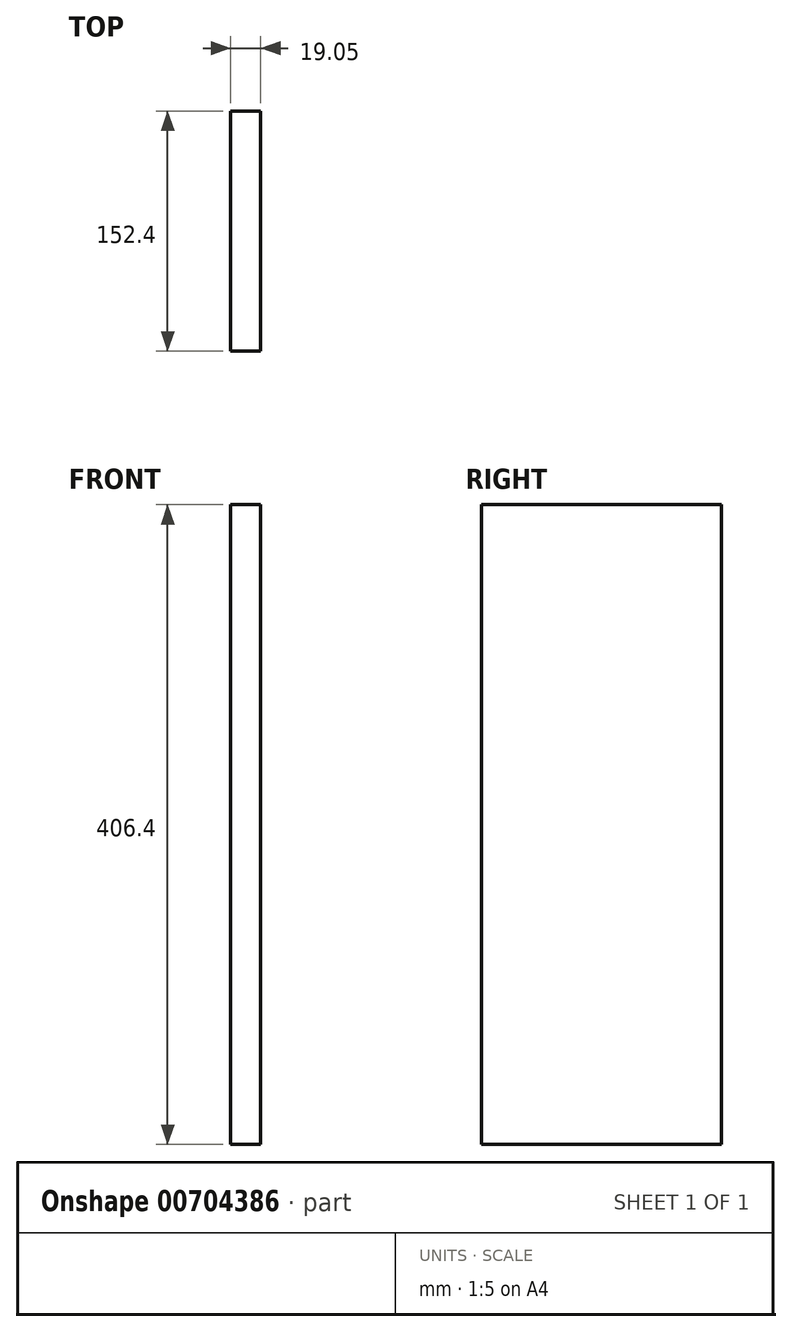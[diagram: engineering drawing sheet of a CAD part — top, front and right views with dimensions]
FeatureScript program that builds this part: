
annotation { "Feature Type Name" : "Feature", "Feature Type Description" : "" }
export const myFeature = defineFeature(function(context is Context, id is Id, definition is map)
    precondition{}
    {
        {
            var Q0;
            Q0=qCreatedBy(makeId("Right.planeOp"),FACE);
            var sketch = newSketch(context, id + "F0", { "sketchPlane" : qUnion([Q0])});
            skLineSegment(sketch, "E0.bottom", {"start": v(76.2, 203.2) * mm, "end": v(-76.2, 203.2) * mm});
            skLineSegment(sketch, "E0.top", {"start": v(76.2, -203.2) * mm, "end": v(-76.2, -203.2) * mm});
            skLineSegment(sketch, "E0.left", {"start": v(76.2, 203.2) * mm, "end": v(76.2, -203.2) * mm});
            skLineSegment(sketch, "E0.right", {"start": v(-76.2, 203.2) * mm, "end": v(-76.2, -203.2) * mm});
            skPoint(sketch, "E0.middle", {"position": v(0, 0) * mm});
            skSolve(sketch);
        }
        {
            var Q0;
            Q0=makeQuery(id+"F0.imprint","IMPRINT",FACE,{"disambiguationData":[TD([[makeQuery(id+"F0.imprint","IMPRINT",EDGE,{"derivedFrom":sQuery(id+"F0.wireOp",EDGE,"E0.bottom")}),1.0]])]});
            extrude(context, id + "F1", {"entities" : qUnion([Q0]), "depth" : 19.05 * mm, "offsetDistance" : 25.4 * mm});
        }
    });
